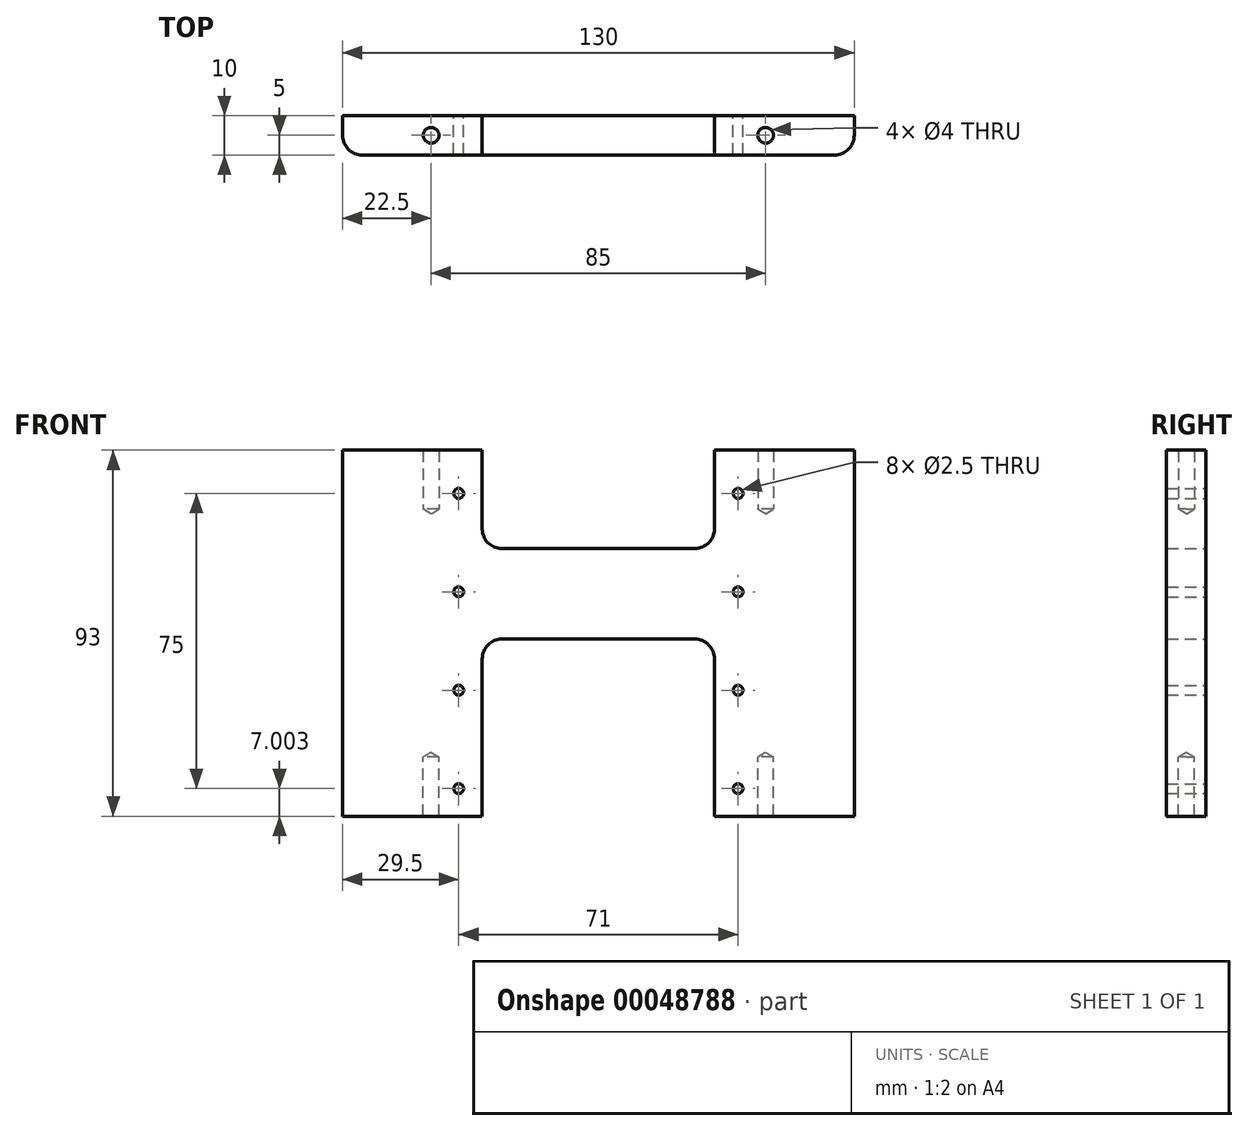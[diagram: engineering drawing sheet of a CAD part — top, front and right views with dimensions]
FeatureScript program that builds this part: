
annotation { "Feature Type Name" : "Feature", "Feature Type Description" : "" }
export const myFeature = defineFeature(function(context is Context, id is Id, definition is map)
    precondition{}
    {
        {
            var Q0;
            Q0=qCreatedBy(makeId("Front.planeOp"),FACE);
            var sketch = newSketch(context, id + "F0", { "sketchPlane" : qUnion([Q0])});
            skLineSegment(sketch, "E0.right", {"start": v(-65, -49.67) * mm, "end": v(-65, 43.33) * mm});
            skPoint(sketch, "E0.middle", {"position": v(0, 0) * mm});
            skLineSegment(sketch, "E1.top", {"start": v(-29.5, -4.67) * mm, "end": v(0, -4.67) * mm});
            skLineSegment(sketch, "E1.left", {"start": v(-29.5, -49.67) * mm, "end": v(-29.5, -4.67) * mm});
            skLineSegment(sketch, "E2", {"start": v(-65, -49.67) * mm, "end": v(-29.5, -49.67) * mm});
            skLineSegment(sketch, "E3.top", {"start": v(-29.5, 18.33) * mm, "end": v(0, 18.33) * mm});
            skLineSegment(sketch, "E3.left", {"start": v(-29.5, 43.33) * mm, "end": v(-29.5, 18.33) * mm});
            skLineSegment(sketch, "E4", {"start": v(-65, 43.33) * mm, "end": v(-29.5, 43.33) * mm});
            skLineSegment(sketch, "E5", {"start": v(0, 18.33) * mm, "end": v(0, -4.67) * mm});
            skCircle(sketch, "E6", {"center": v(-35.5, 32.33) * mm, "radius": 1.25 * mm});
            skCircle(sketch, "E7.0.1.0", {"center": v(-35.5, 7.33) * mm, "radius": 1.25 * mm});
            skCircle(sketch, "E7.0.2.0", {"center": v(-35.5, -17.67) * mm, "radius": 1.25 * mm});
            skLineSegment(sketch, "E7.direction1", {"start": v(-35.5, 32.33) * mm, "end": v(-10.5, 32.33) * mm, "construction": true});
            skLineSegment(sketch, "E7.direction2", {"start": v(-35.5, 32.33) * mm, "end": v(-35.5, 7.33) * mm, "construction": true});
            skCircle(sketch, "E8.0.0.3", {"center": v(-35.5, -42.67) * mm, "radius": 1.25 * mm});
            skSolve(sketch);
        }
        {
            var Q0;
            Q0=makeQuery(id+"F0.imprint","IMPRINT",FACE,{"disambiguationData":[TD([[makeQuery(id+"F0.imprint","IMPRINT",EDGE,{"derivedFrom":sQuery(id+"F0.wireOp",EDGE,"E0.right")}),-1.0]])]});
            extrude(context, id + "F1", {"entities" : qUnion([Q0]), "depth" : 10 * mm});
        }
        {
            var Q0;
            Q0=makeQuery(id+"F1.opExtrude","CAP_EDGE",EDGE,{"disambiguationData":[OSD([sQuery(id+"F0.wireOp",EDGE,"E0.right")])],"isStart":false});
            var Q1;
            Q1=makeQuery(id+"F1.opExtrude","SWEPT_EDGE",EDGE,{"disambiguationData":[OSD([sQuery(id+"F0.wireOp",EDGE,"E1.top"),sQuery(id+"F0.wireOp",EDGE,"E1.left")])]});
            var Q2;
            Q2=makeQuery(id+"F1.opExtrude","SWEPT_EDGE",EDGE,{"disambiguationData":[OSD([sQuery(id+"F0.wireOp",EDGE,"E3.top"),sQuery(id+"F0.wireOp",EDGE,"E3.left")])]});
            fillet(context, id + "F2", {"entities" : qUnion([Q0, Q1, Q2]), "radius" : 5 * mm, "tangentPropagation" : true, "allowEdgeOverflow" : false});
        }
        {
            var Q0;
            Q0=makeQuery(id+"F1.opExtrude","SWEPT_FACE",FACE,{"disambiguationData":[OSD([sQuery(id+"F0.wireOp",EDGE,"E4")])]});
            var sketch = newSketch(context, id + "F3", { "sketchPlane" : qUnion([Q0])});
            skPoint(sketch, "E9", {"position": v(-42.5, -5) * mm});
            skPoint(sketch, "E9.positionSnap0", {"position": v(-29.5, -5) * mm});
            skSolve(sketch);
        }
        {
            var Q0;
            Q0=makeQuery(id+"F1.opExtrude","SWEPT_FACE",FACE,{"disambiguationData":[OSD([sQuery(id+"F0.wireOp",EDGE,"E2")])]});
            var sketch = newSketch(context, id + "F4", { "sketchPlane" : qUnion([Q0])});
            skPoint(sketch, "E10", {"position": v(-42.5, 5) * mm});
            skPoint(sketch, "E10.positionSnap0", {"position": v(-29.5, 5) * mm});
            skSolve(sketch);
        }
        {
            var Q0;
            Q0=sQuery(id+"F3.wireOp",VERTEX,"E9");
            var Q1;
            Q1=sQuery(id+"F4.wireOp",VERTEX,"E10");
            var Q2;
            Q2=makeQuery(id+"F1.opExtrude","SWEPT_BODY",BODY,{"disambiguationData":[OSD([sQuery(id+"F0.wireOp",EDGE,"E0.left"),sQuery(id+"F0.wireOp",EDGE,"E0.right"),sQuery(id+"F0.wireOp",EDGE,"E1.top"),sQuery(id+"F0.wireOp",EDGE,"E1.left"),sQuery(id+"F0.wireOp",EDGE,"E1.right"),sQuery(id+"F0.wireOp",EDGE,"E2"),sQuery(id+"F0.wireOp",EDGE,"GQXs4lhv-NWdz-ZINx-7NqH-gZMI4iZZZFkd"),sQuery(id+"F0.wireOp",EDGE,"E3.top"),sQuery(id+"F0.wireOp",EDGE,"E3.left"),sQuery(id+"F0.wireOp",EDGE,"E3.right"),sQuery(id+"F0.wireOp",EDGE,"E4"),sQuery(id+"F0.wireOp",EDGE,"TXQTB2sG-kFcx-ucT4-4UpO-mhL2eI2gHOT6")])]});
            hole(context, id + "F5", {"style" : HoleStyle.SIMPLE, "endStyle" : HoleEndStyle.BLIND, "standardTappedOrClearance" : lookupTablePath({ "standard" : "ISO", "engagement" : "75%", "pitch" : "1 mm", "size" : "M5", "type" : "Tapped" }), "standardBlindInLast" : lookupTablePath({ "standard" : "ISO", "engagement" : "75%", "pitch" : "1 mm", "size" : "M5", "type" : "Tapped" }), "holeDiameter" : 4 * mm, "holeDepth" : 15 * mm, "locations" : qUnion([Q0, Q1]), "scope" : qUnion([Q2]), "startStyle" : HoleStartStyle.PART});
        }
        {
            var Q0;
            Q0=makeQuery(id+"F1.opExtrude","SWEPT_BODY",BODY,{"disambiguationData":[OSD([sQuery(id+"F0.wireOp",EDGE,"E0.right"),sQuery(id+"F0.wireOp",EDGE,"E1.top"),sQuery(id+"F0.wireOp",EDGE,"E1.left"),sQuery(id+"F0.wireOp",EDGE,"E2"),sQuery(id+"F0.wireOp",EDGE,"E3.top"),sQuery(id+"F0.wireOp",EDGE,"E3.left"),sQuery(id+"F0.wireOp",EDGE,"E4"),sQuery(id+"F0.wireOp",EDGE,"E5")])]});
            var Q1;
            Q1=qCreatedBy(makeId("Right.planeOp"),FACE);
            mirror(context, id + "F6", {"operationType" : NewBodyOperationType.ADD, "entities" : qUnion([Q0]), "mirrorPlane" : qUnion([Q1])});
        }
    });
